# Revit family: Salda Indoor Vertical AHU.Smarty Series
name_source: partatom
category: Mechanical Equipment
revit_build: Autodesk Revit 2016 (Build: 20150220_1215(x64)
units: mm (PartAtom-declared; Revit-internal decimal feet)

## family parameters
Always vertical = Yes
Cut with Voids When Loaded = No
OmniClass Number = 23.75.35.14.11
OmniClass Title = Built-Up Indoor Air Handling Units
Part Type = Normal
Room Calculation Point = No
Round Connector Dimension = Use Diameter
Shared = No
Work Plane-Based = Yes

## types (6) — shared parameters
Default Elevation = 1219 mm
Manufacturer = Salda
URL = http://salda.lt
Unit Mass = 39.00 kg
Voltage = 230 V

## per-type parameters (varying)
| type | Connector Back Horizontal Offset | Connector Front Horizontal Offset | Connector Height | Current | Drainage Pipe Front Offset | Drainage Pipe Right Offset | Electrical Box Length | L1 | L2 | L3 | L4 | Maximum Flow Rate | Module Height | Overall Height | Overall Length | Overall Width | Power | Service Zone Width | Type |
| Smarty 3X V 1.1 | 170 mm  [stored 0.557743 ft] | 116 mm  [stored 0.380577 ft] | 80 mm  [stored 0.262467 ft] | 7 A | 408 mm | 258 mm  [stored 0.846457 ft] | 183 mm | 110 mm  [stored 0.360892 ft] | 113 mm  [stored 0.370735 ft] | 110 mm  [stored 0.360892 ft] | 265 mm  [stored 0.869423 ft] | 445.0 m³/h | 810 mm | 890 mm  [stored 2.91995 ft] | 599 mm  [stored 1.96522 ft] | 538 mm  [stored 1.76509 ft] | 1370 W | 807 mm  [stored 2.64764 ft] | 3 |
| Smarty 3X V 1.2 | 170 mm  [stored 0.557743 ft] | 116 mm  [stored 0.380577 ft] | 80 mm  [stored 0.262467 ft] | 2 A | 408 mm | 258 mm  [stored 0.846457 ft] | 183 mm | 110 mm  [stored 0.360892 ft] | 113 mm  [stored 0.370735 ft] | 110 mm  [stored 0.360892 ft] | 265 mm  [stored 0.869423 ft] | 445.0 m³/h | 810 mm | 890 mm  [stored 2.91995 ft] | 599 mm  [stored 1.96522 ft] | 538 mm  [stored 1.76509 ft] | 170 W | 807 mm  [stored 2.64764 ft] | 3 |
| Smarty 4X V 1.1 | 170 mm  [stored 0.557743 ft] | 116 mm  [stored 0.380577 ft] | 80 mm  [stored 0.262467 ft] | 7 A | 284 mm  [stored 0.931759 ft] | 193 mm  [stored 0.633202 ft] | 183 mm | 110 mm  [stored 0.360892 ft] | 113 mm  [stored 0.370735 ft] | 110 mm  [stored 0.360892 ft] | 265 mm  [stored 0.869423 ft] | 595.0 m³/h | 810 mm | 890 mm  [stored 2.91995 ft] | 599 mm  [stored 1.96522 ft] | 538 mm  [stored 1.76509 ft] | 1620 W | 807 mm  [stored 2.64764 ft] | 4 |
| Smarty 4X V 1.2 | 170 mm  [stored 0.557743 ft] | 116 mm  [stored 0.380577 ft] | 80 mm  [stored 0.262467 ft] | 2 A | 284 mm  [stored 0.931759 ft] | 193 mm  [stored 0.633202 ft] | 183 mm | 110 mm  [stored 0.360892 ft] | 113 mm  [stored 0.370735 ft] | 110 mm  [stored 0.360892 ft] | 265 mm  [stored 0.869423 ft] | 595.0 m³/h | 810 mm | 890 mm  [stored 2.91995 ft] | 599 mm  [stored 1.96522 ft] | 538 mm  [stored 1.76509 ft] | 420 W | 807 mm  [stored 2.64764 ft] | 4 |
| Smarty 2X V 1.1 | 79 mm | 82 mm  [stored 0.269029 ft] | 35 mm  [stored 0.114829 ft] | 3 A | 156 mm  [stored 0.511811 ft] | 209 mm  [stored 0.685696 ft] | 120 mm  [stored 0.393701 ft] | 83 mm  [stored 0.27231 ft] | 82 mm  [stored 0.269029 ft] | 195 mm  [stored 0.639764 ft] | 242 mm  [stored 0.793963 ft] | 211.0 m³/h | 697 mm  [stored 2.28675 ft] | 732 mm | 595 mm  [stored 1.9521 ft] | 316 mm | 670 W | 474 mm | 2 |
| Smarty 2X V 1.2 | 79 mm | 82 mm  [stored 0.269029 ft] | 35 mm  [stored 0.114829 ft] | 1 A | 156 mm  [stored 0.511811 ft] | 209 mm  [stored 0.685696 ft] | 120 mm  [stored 0.393701 ft] | 83 mm  [stored 0.27231 ft] | 82 mm  [stored 0.269029 ft] | 195 mm  [stored 0.639764 ft] | 242 mm  [stored 0.793963 ft] | 211.0 m³/h | 697 mm  [stored 2.28675 ft] | 732 mm | 595 mm  [stored 1.9521 ft] | 316 mm | 70 W | 474 mm | 2 |

note: column(s) folded — value = type name in every type: Model

note: [stored X ft] marks values corroborated as IEEE doubles in the binary element streams (Revit-internal decimal feet)

## geometry (parser evidence)
native form markers: Sweep x5
no freeform markers — native parametric forms only
